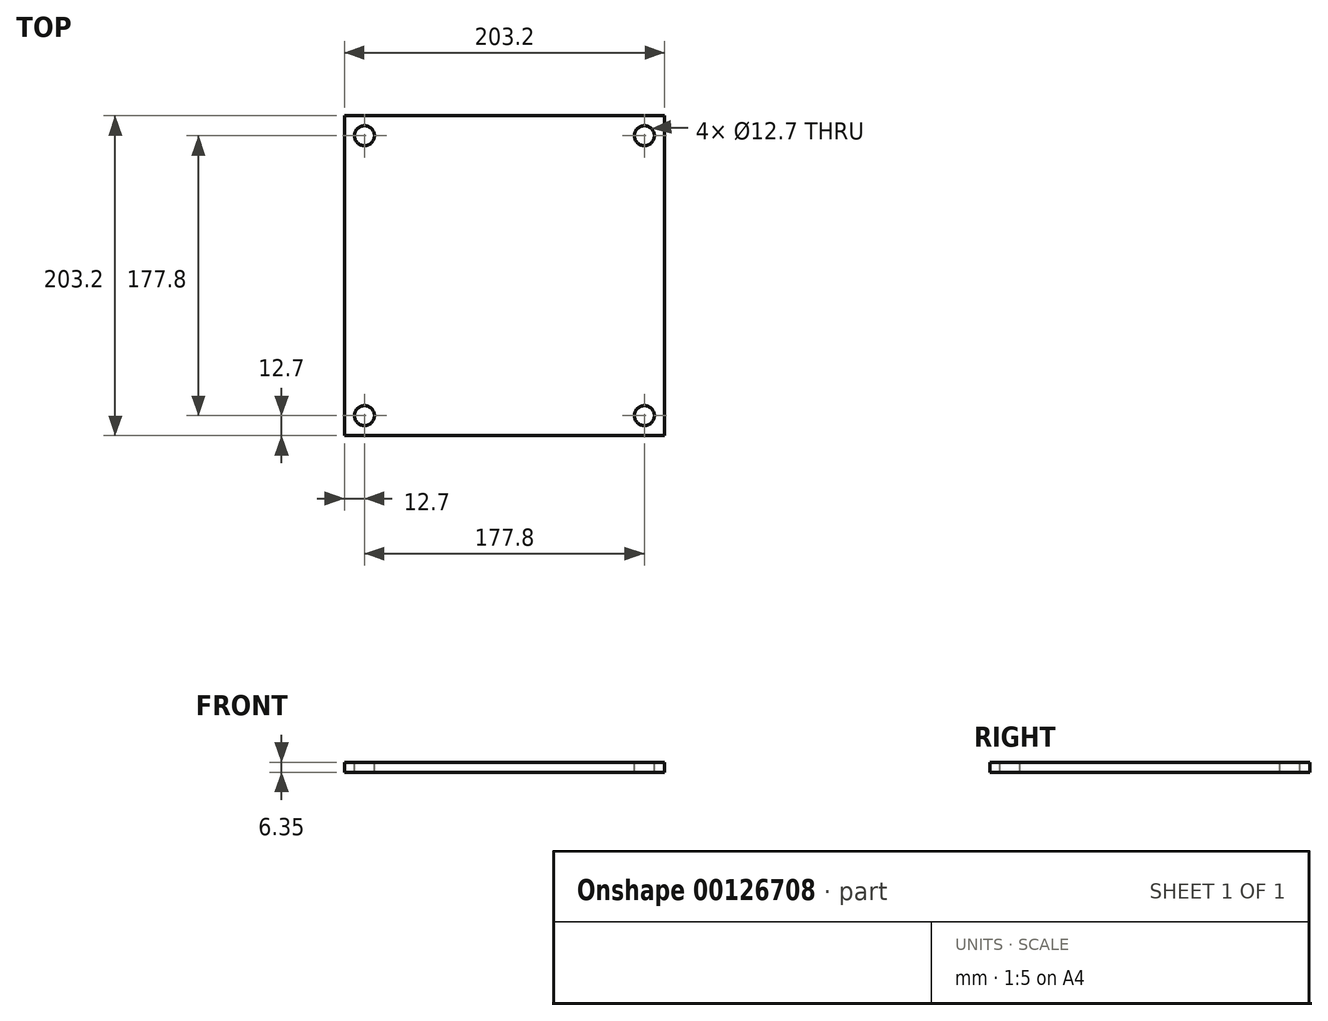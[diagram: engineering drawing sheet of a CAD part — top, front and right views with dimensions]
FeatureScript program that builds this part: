
annotation { "Feature Type Name" : "Feature", "Feature Type Description" : "" }
export const myFeature = defineFeature(function(context is Context, id is Id, definition is map)
    precondition{}
    {
        {
            var Q0;
            Q0=qCreatedBy(makeId("Top.planeOp"),FACE);
            var sketch = newSketch(context, id + "F0", { "sketchPlane" : qUnion([Q0])});
            skLineSegment(sketch, "E0.bottom", {"start": v(0, 0) * mm, "end": v(203.2, 0) * mm});
            skLineSegment(sketch, "E0.top", {"start": v(0, 203.2) * mm, "end": v(203.2, 203.2) * mm});
            skLineSegment(sketch, "E0.left", {"start": v(0, 0) * mm, "end": v(0, 203.2) * mm});
            skLineSegment(sketch, "E0.right", {"start": v(203.2, 0) * mm, "end": v(203.2, 203.2) * mm});
            skSolve(sketch);
        }
        {
            var Q0;
            Q0=makeQuery(id+"F0.imprint","IMPRINT",FACE,{"disambiguationData":[TD([[makeQuery(id+"F0.imprint","IMPRINT",EDGE,{"derivedFrom":sQuery(id+"F0.wireOp",EDGE,"E0.bottom")}),1.0]])]});
            extrude(context, id + "F1", {"entities" : qUnion([Q0]), "depth" : 6.35 * mm});
        }
        {
            var Q0;
            Q0=makeQuery(id+"F1.opExtrude","CAP_FACE",FACE,{"disambiguationData":[OSD([sQuery(id+"F0.wireOp",EDGE,"E0.bottom"),sQuery(id+"F0.wireOp",EDGE,"E0.top"),sQuery(id+"F0.wireOp",EDGE,"E0.left"),sQuery(id+"F0.wireOp",EDGE,"E0.right")])],"isStart":false});
            var sketch = newSketch(context, id + "F2", { "sketchPlane" : qUnion([Q0])});
            skLineSegment(sketch, "E1.0", {"start": v(12.7, 0) * mm, "end": v(12.7, 203.2) * mm});
            skLineSegment(sketch, "E2.0", {"start": v(209.55, 0) * mm, "end": v(209.55, 203.2) * mm});
            skLineSegment(sketch, "E3.0", {"start": v(0, 12.7) * mm, "end": v(203.2, 12.7) * mm});
            skLineSegment(sketch, "E4.0", {"start": v(190.5, 0) * mm, "end": v(190.5, 203.2) * mm});
            skLineSegment(sketch, "E5.0", {"start": v(0, 190.5) * mm, "end": v(203.2, 190.5) * mm});
            skCircle(sketch, "E6", {"center": v(12.7, 190.5) * mm, "radius": 6.35 * mm});
            skCircle(sketch, "E7", {"center": v(12.7, 12.7) * mm, "radius": 6.35 * mm});
            skCircle(sketch, "E8", {"center": v(190.5, 190.5) * mm, "radius": 6.35 * mm});
            skCircle(sketch, "E9", {"center": v(190.5, 12.7) * mm, "radius": 6.35 * mm});
            skSolve(sketch);
        }
        {
            var Q0;
            Q0=sQuery(id+"F2.wireOp",VERTEX,"E6.center");
            var Q1;
            Q1=sQuery(id+"F2.wireOp",VERTEX,"E7.center");
            var Q2;
            Q2=sQuery(id+"F2.wireOp",VERTEX,"E9.center");
            var Q3;
            Q3=sQuery(id+"F2.wireOp",VERTEX,"E8.center");
            var Q4;
            Q4=makeQuery(id+"F1.opExtrude","SWEPT_BODY",BODY,{"disambiguationData":[OSD([sQuery(id+"F0.wireOp",EDGE,"E0.bottom"),sQuery(id+"F0.wireOp",EDGE,"E0.top"),sQuery(id+"F0.wireOp",EDGE,"E0.left"),sQuery(id+"F0.wireOp",EDGE,"E0.right")])]});
            hole(context, id + "F3", {"style" : HoleStyle.SIMPLE, "endStyle" : HoleEndStyle.THROUGH, "holeDiameter" : 12.7 * mm, "locations" : qUnion([Q0, Q1, Q2, Q3]), "scope" : qUnion([Q4]), "isTappedThrough" : true});
        }
    });
